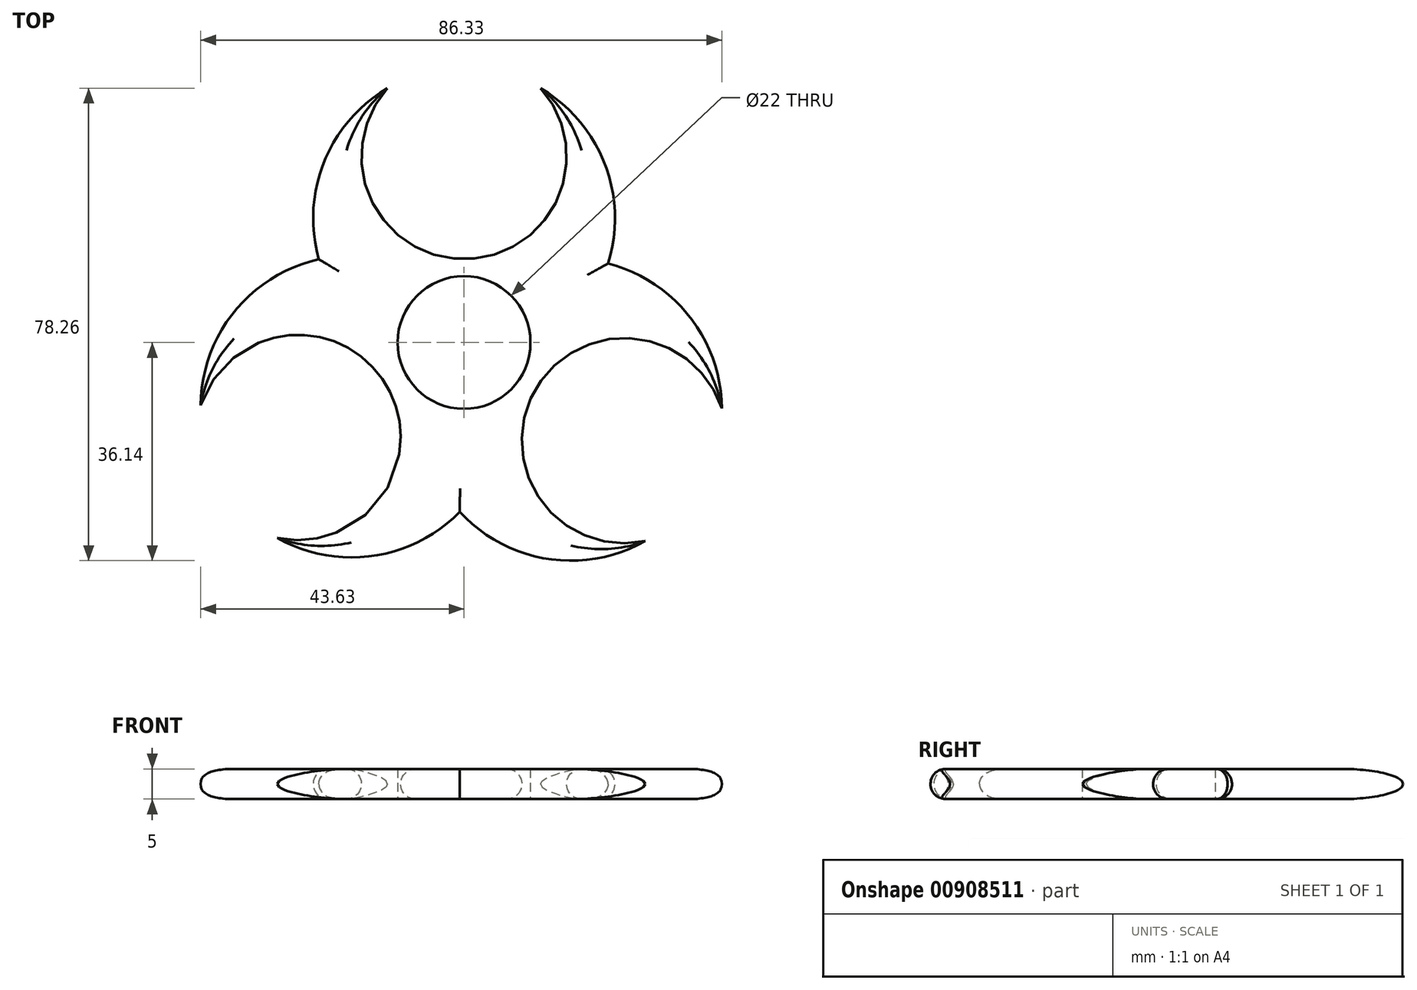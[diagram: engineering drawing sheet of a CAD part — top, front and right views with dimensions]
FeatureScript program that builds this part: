
annotation { "Feature Type Name" : "Feature", "Feature Type Description" : "" }
export const myFeature = defineFeature(function(context is Context, id is Id, definition is map)
    precondition{}
    {
        {
            var Q0;
            Q0=qCreatedBy(makeId("Top.planeOp"),FACE);
            var sketch = newSketch(context, id + "F0", { "sketchPlane" : qUnion([Q0])});
            skCircle(sketch, "E0", {"center": v(0, 0) * mm, "radius": 11 * mm});
            skArc(sketch, "E1", {"start": v(-12.7, 42.12) * mm, "mid": v(0, 13.82) * mm, "end": v(12.7, 42.12) * mm});
            skArc(sketch, "E2", {"start": v(-12.7, 42.12) * mm, "mid": v(-23.2, 29.89) * mm, "end": v(-24.06, 13.8) * mm});
            skArc(sketch, "E3.trimOffspring", {"start": v(23.85, 13.09) * mm, "mid": v(23.34, 29.54) * mm, "end": v(12.7, 42.12) * mm});
            skArc(sketch, "E4.1.0", {"start": v(-30.92, -32.37) * mm, "mid": v(-15.09, -35.36) * mm, "end": v(-0.72, -28.05) * mm});
            skArc(sketch, "E4.1.1", {"start": v(-30.92, -32.37) * mm, "mid": v(-12.77, -7.22) * mm, "end": v(-43.63, -10.37) * mm});
            skArc(sketch, "E4.1.2", {"start": v(-24.06, 13.8) * mm, "mid": v(-38.06, 5.12) * mm, "end": v(-43.63, -10.37) * mm});
            skArc(sketch, "E4.2.0", {"start": v(42.7, -10.91) * mm, "mid": v(37.36, 4.3) * mm, "end": v(23.85, 13.09) * mm});
            skArc(sketch, "E4.2.1", {"start": v(42.7, -10.91) * mm, "mid": v(11.84, -7.76) * mm, "end": v(30, -32.91) * mm});
            skArc(sketch, "E4.2.2", {"start": v(-0.72, -28.05) * mm, "mid": v(13.8, -35.84) * mm, "end": v(30, -32.91) * mm});
            skPoint(sketch, "E4.center", {"position": v(-0.3, -0.4) * mm});
            skPoint(sketch, "E5.orphan", {"position": v(-4.52, 10.03) * mm});
            skPoint(sketch, "E6.orphan", {"position": v(-10.83, -1.95) * mm});
            skPoint(sketch, "E7.orphan", {"position": v(10.83, -1.95) * mm});
            skPoint(sketch, "E8.orphan", {"position": v(6.3, -8.72) * mm});
            skPoint(sketch, "E9.orphan", {"position": v(-7.23, -9.25) * mm});
            skSolve(sketch);
        }
        {
            var Q0;
            Q0 = qSketchRegion(id + "F0", true);
            extrude(context, id + "F1", {"entities" : qUnion([Q0]), "endBound" : BoundingType.SYMMETRIC, "depth" : 5 * mm, "offsetDistance" : 25 * mm});
        }
        {
            var Q0;
            Q0=makeQuery(id+"F1.opExtrude","CAP_EDGE",EDGE,{"disambiguationData":[OSD([sQuery(id+"F0.wireOp",EDGE,"E4.2.1")])],"isStart":false});
            var Q1;
            Q1=makeQuery(id+"F1.opExtrude","CAP_EDGE",EDGE,{"disambiguationData":[OSD([sQuery(id+"F0.wireOp",EDGE,"E4.2.2")])],"isStart":false});
            var Q2;
            Q2=makeQuery(id+"F1.opExtrude","CAP_EDGE",EDGE,{"disambiguationData":[OSD([sQuery(id+"F0.wireOp",EDGE,"E4.1.0")])],"isStart":false});
            var Q3;
            Q3=makeQuery(id+"F1.opExtrude","CAP_EDGE",EDGE,{"disambiguationData":[OSD([sQuery(id+"F0.wireOp",EDGE,"E4.1.1")])],"isStart":false});
            var Q4;
            Q4=makeQuery(id+"F1.opExtrude","CAP_EDGE",EDGE,{"disambiguationData":[OSD([sQuery(id+"F0.wireOp",EDGE,"E4.1.2")])],"isStart":false});
            var Q5;
            Q5=makeQuery(id+"F1.opExtrude","CAP_EDGE",EDGE,{"disambiguationData":[OSD([sQuery(id+"F0.wireOp",EDGE,"E2")])],"isStart":false});
            var Q6;
            Q6=makeQuery(id+"F1.opExtrude","CAP_EDGE",EDGE,{"disambiguationData":[OSD([sQuery(id+"F0.wireOp",EDGE,"E1")])],"isStart":false});
            var Q7;
            Q7=makeQuery(id+"F1.opExtrude","CAP_EDGE",EDGE,{"disambiguationData":[OSD([sQuery(id+"F0.wireOp",EDGE,"E3.trimOffspring")])],"isStart":false});
            var Q8;
            Q8=makeQuery(id+"F1.opExtrude","CAP_EDGE",EDGE,{"disambiguationData":[OSD([sQuery(id+"F0.wireOp",EDGE,"E4.2.0")])],"isStart":false});
            var Q9;
            Q9=makeQuery(id+"F1.opExtrude","CAP_EDGE",EDGE,{"disambiguationData":[OSD([sQuery(id+"F0.wireOp",EDGE,"E4.2.2")])],"isStart":true});
            var Q10;
            Q10=makeQuery(id+"F1.opExtrude","CAP_EDGE",EDGE,{"disambiguationData":[OSD([sQuery(id+"F0.wireOp",EDGE,"E4.1.0")])],"isStart":true});
            var Q11;
            Q11=makeQuery(id+"F1.opExtrude","CAP_EDGE",EDGE,{"disambiguationData":[OSD([sQuery(id+"F0.wireOp",EDGE,"E4.1.1")])],"isStart":true});
            var Q12;
            Q12=makeQuery(id+"F1.opExtrude","CAP_EDGE",EDGE,{"disambiguationData":[OSD([sQuery(id+"F0.wireOp",EDGE,"E4.1.2")])],"isStart":true});
            var Q13;
            Q13=makeQuery(id+"F1.opExtrude","CAP_EDGE",EDGE,{"disambiguationData":[OSD([sQuery(id+"F0.wireOp",EDGE,"E2")])],"isStart":true});
            var Q14;
            Q14=makeQuery(id+"F1.opExtrude","CAP_EDGE",EDGE,{"disambiguationData":[OSD([sQuery(id+"F0.wireOp",EDGE,"E1")])],"isStart":true});
            var Q15;
            Q15=makeQuery(id+"F1.opExtrude","CAP_EDGE",EDGE,{"disambiguationData":[OSD([sQuery(id+"F0.wireOp",EDGE,"E4.2.0")])],"isStart":true});
            var Q16;
            Q16=makeQuery(id+"F1.opExtrude","CAP_EDGE",EDGE,{"disambiguationData":[OSD([sQuery(id+"F0.wireOp",EDGE,"E4.2.1")])],"isStart":true});
            var Q17;
            Q17=makeQuery(id+"F1.opExtrude","CAP_EDGE",EDGE,{"disambiguationData":[OSD([sQuery(id+"F0.wireOp",EDGE,"E3.trimOffspring")])],"isStart":true});
            fillet(context, id + "F2", {"entities" : qUnion([Q0, Q1, Q2, Q3, Q4, Q5, Q6, Q7, Q8, Q9, Q10, Q11, Q12, Q13, Q14, Q15, Q16, Q17]), "radius" : 2.5 * mm, "tangentPropagation" : true, "allowEdgeOverflow" : false});
        }
    });
